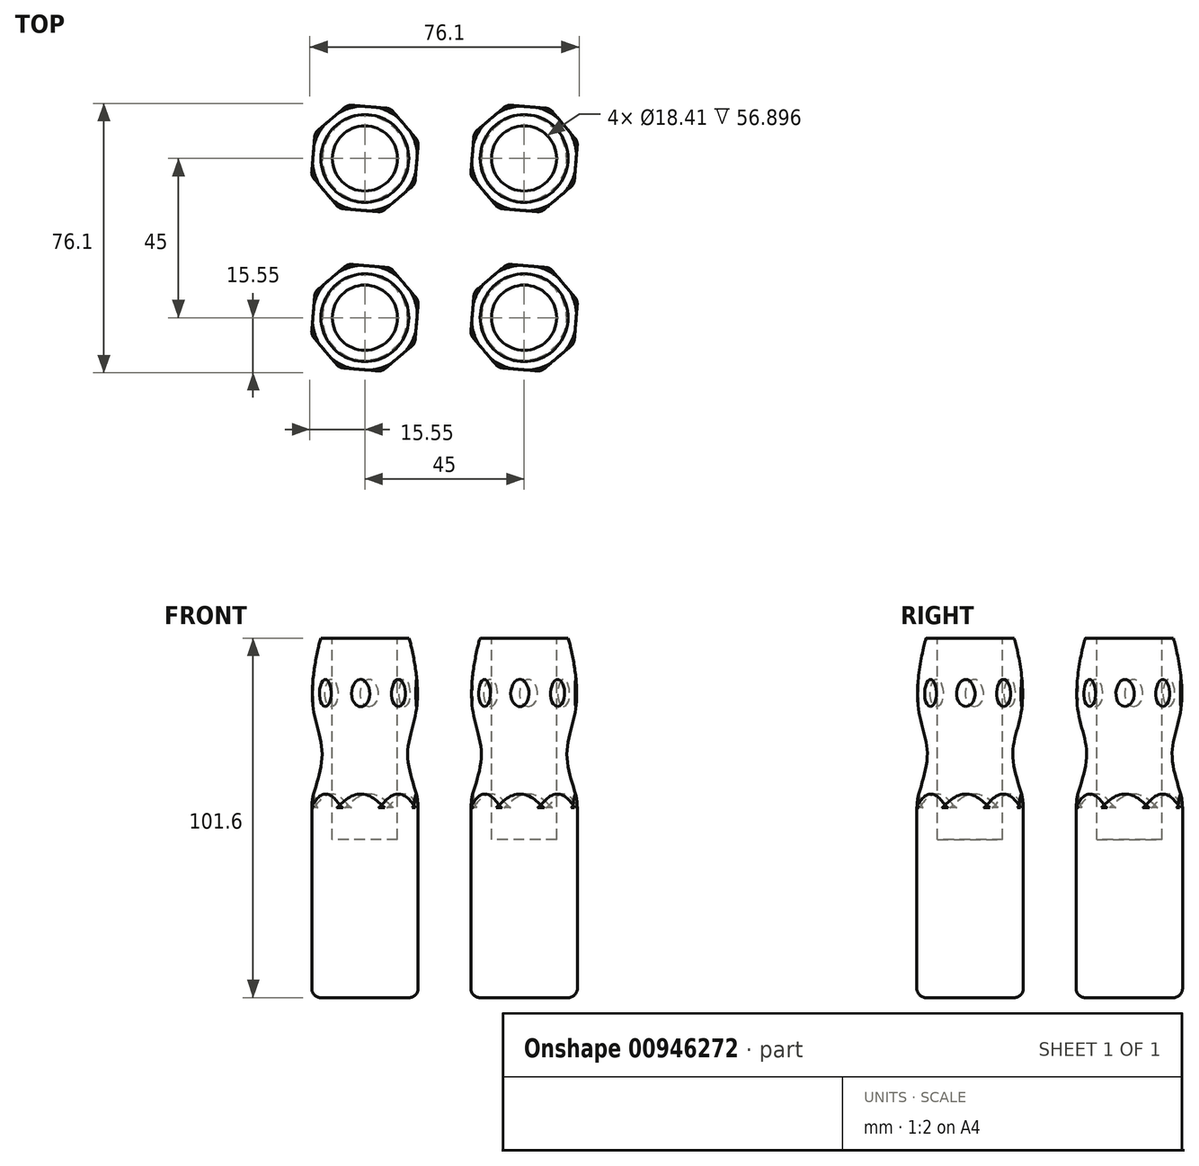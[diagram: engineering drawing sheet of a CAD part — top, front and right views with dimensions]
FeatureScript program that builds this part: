
annotation { "Feature Type Name" : "Feature", "Feature Type Description" : "" }
export const myFeature = defineFeature(function(context is Context, id is Id, definition is map)
    precondition{}
    {
        {
            var Q0;
            Q0=qCreatedBy(makeId("Top.planeOp"),FACE);
            var sketch = newSketch(context, id + "F0", { "sketchPlane" : qUnion([Q0])});
            skLineSegment(sketch, "E0.0", {"start": v(-4.85, 15.12) * mm, "end": v(7.26, 14.12) * mm});
            skLineSegment(sketch, "E0.1", {"start": v(7.26, 14.12) * mm, "end": v(15.12, 4.85) * mm});
            skLineSegment(sketch, "E0.2", {"start": v(15.12, 4.85) * mm, "end": v(14.12, -7.26) * mm});
            skLineSegment(sketch, "E0.3", {"start": v(14.12, -7.26) * mm, "end": v(4.85, -15.12) * mm});
            skLineSegment(sketch, "E0.4", {"start": v(4.85, -15.12) * mm, "end": v(-7.26, -14.12) * mm});
            skLineSegment(sketch, "E0.5", {"start": v(-7.26, -14.12) * mm, "end": v(-15.12, -4.85) * mm});
            skLineSegment(sketch, "E0.6", {"start": v(-15.12, -4.85) * mm, "end": v(-14.12, 7.26) * mm});
            skLineSegment(sketch, "E0.7", {"start": v(-14.12, 7.26) * mm, "end": v(-4.85, 15.12) * mm});
            skSolve(sketch);
        }
        {
            var Q0;
            Q0=makeQuery(id+"F0.imprint","IMPRINT",FACE,{"disambiguationData":[TD([[makeQuery(id+"F0.imprint","IMPRINT",EDGE,{"derivedFrom":sQuery(id+"F0.wireOp",EDGE,"e4fd1291-5814-49df-8d21-47046975691b.0")}),-1.0]])]});
            var Q1;
            Q1=makeQuery(id+"F0.imprint","IMPRINT",FACE,{"disambiguationData":[TD([[makeQuery(id+"F0.imprint","IMPRINT",EDGE,{"derivedFrom":sQuery(id+"F0.wireOp",EDGE,"E0.0")}),-1.0]])]});
            extrude(context, id + "F1", {"entities" : qUnion([Q0, Q1]), "depth" : 101.6 * mm, "offsetDistance" : 25.4 * mm});
        }
        {
            var Q0;
            Q0=qCreatedBy(makeId("Right.planeOp"),FACE);
            var sketch = newSketch(context, id + "F2", { "sketchPlane" : qUnion([Q0])});
            skLineSegment(sketch, "E1", {"start": v(0, 0) * mm, "end": v(-15.88, 0) * mm});
            skLineSegment(sketch, "E2", {"start": v(-15.88, 0) * mm, "end": v(-15.88, 53.34) * mm});
            skFitSpline(sketch, "E3", {"points": [v(-15.88, 53.34) * mm, v(-12.12, 69.77) * mm, v(-14.9, 85.44) * mm, v(-12.36, 101.7) * mm], "startDerivative": vector(18.24, 59.15) * mm, "endDerivative": vector(2.93, 2.79) * mm});
            skLineSegment(sketch, "E4", {"start": v(-12.36, 101.7) * mm, "end": v(-18.05, 101.7) * mm});
            skLineSegment(sketch, "E5", {"start": v(-18.05, 101.7) * mm, "end": v(-18.97, 0) * mm});
            skLineSegment(sketch, "E6", {"start": v(-18.97, 0) * mm, "end": v(-15.88, 0) * mm});
            skLineSegment(sketch, "E7", {"start": v(0, 0) * mm, "end": v(0, 84.28) * mm});
            skSolve(sketch);
        }
        {
            var Q0;
            Q0=makeQuery(id+"F2.imprint","IMPRINT",FACE,{"disambiguationData":[TD([[makeQuery(id+"F2.imprint","IMPRINT",EDGE,{"derivedFrom":sQuery(id+"F2.wireOp",EDGE,"E2")}),1.0]])]});
            var Q1;
            Q1=sQuery(id+"F2.wireOp",EDGE,"E7");
            revolve(context, id + "F3", {"operationType" : NewBodyOperationType.REMOVE, "surfaceOperationType" : NewSurfaceOperationType.NEW, "entities" : qUnion([Q0]), "axis" : qUnion([Q1]), "revolveType" : RevolveType.FULL, "oppositeDirection" : true});
        }
        {
            var Q0;
            Q0=makeQuery(id+"F1.opExtrude","CAP_FACE",FACE,{"disambiguationData":[OSD([sQuery(id+"F0.wireOp",EDGE,"E0.0"),sQuery(id+"F0.wireOp",EDGE,"E0.1"),sQuery(id+"F0.wireOp",EDGE,"E0.2"),sQuery(id+"F0.wireOp",EDGE,"E0.3"),sQuery(id+"F0.wireOp",EDGE,"E0.4"),sQuery(id+"F0.wireOp",EDGE,"E0.5"),sQuery(id+"F0.wireOp",EDGE,"E0.6"),sQuery(id+"F0.wireOp",EDGE,"E0.7")])],"isStart":false});
            var sketch = newSketch(context, id + "F4", { "sketchPlane" : qUnion([Q0])});
            skCircle(sketch, "E8.0.0", {"center": v(0, 0) * mm, "radius": 12.41 * mm});
            skCircle(sketch, "E9", {"center": v(0, 0) * mm, "radius": 9.2 * mm});
            skSolve(sketch);
        }
        {
            var Q0;
            Q0=makeQuery(id+"F4.imprint","IMPRINT",FACE,{"disambiguationData":[TD([[makeQuery(id+"F4.imprint","IMPRINT",EDGE,{"derivedFrom":sQuery(id+"F4.wireOp",EDGE,"E9")}),1.0]])]});
            extrude(context, id + "F5", {"entities" : qUnion([Q0]), "operationType" : NewBodyOperationType.REMOVE, "oppositeDirection" : true, "depth" : 56.9 * mm, "offsetDistance" : 25.4 * mm});
        }
        {
            var Q0;
            {var subQ0=sQuery(id+"F0.wireOp",EDGE,"E0.4");var subQ1=sQuery(id+"F0.wireOp",EDGE,"E0.3");var subQ2=sQuery(id+"F0.wireOp",EDGE,"E0.2");Q0=makeQuery(id+"F3.boolean.opBoolean","SPLIT",FACE,{"disambiguationData":[TD([makeQuery(id+"F1.opExtrude","CAP_FACE",FACE,{"disambiguationData":[OSD([sQuery(id+"F0.wireOp",EDGE,"E0.0"),sQuery(id+"F0.wireOp",EDGE,"E0.1"),subQ2,subQ1,subQ0,sQuery(id+"F0.wireOp",EDGE,"E0.5"),sQuery(id+"F0.wireOp",EDGE,"E0.6"),sQuery(id+"F0.wireOp",EDGE,"E0.7")])],"isStart":true}),makeQuery(id+"F1.opExtrude","SWEPT_FACE",FACE,{"disambiguationData":[OSD([subQ2])]}),makeQuery(id+"F1.opExtrude","SWEPT_FACE",FACE,{"disambiguationData":[OSD([subQ0])]}),makeQuery(id+"F3.opRevolve","SWEPT_FACE",FACE,{"disambiguationData":[OSD([sQuery(id+"F2.wireOp",EDGE,"E3")])]})])],"derivedFrom":makeQuery(id+"F1.opExtrude","SWEPT_FACE",FACE,{"disambiguationData":[OSD([subQ1])]})});}
            var Q1;
            {var subQ0=sQuery(id+"F0.wireOp",EDGE,"E0.5");var subQ1=sQuery(id+"F0.wireOp",EDGE,"E0.4");var subQ2=sQuery(id+"F0.wireOp",EDGE,"E0.3");Q1=makeQuery(id+"F3.boolean.opBoolean","SPLIT",FACE,{"disambiguationData":[TD([makeQuery(id+"F1.opExtrude","CAP_FACE",FACE,{"disambiguationData":[OSD([sQuery(id+"F0.wireOp",EDGE,"E0.0"),sQuery(id+"F0.wireOp",EDGE,"E0.1"),sQuery(id+"F0.wireOp",EDGE,"E0.2"),subQ2,subQ1,subQ0,sQuery(id+"F0.wireOp",EDGE,"E0.6"),sQuery(id+"F0.wireOp",EDGE,"E0.7")])],"isStart":true}),makeQuery(id+"F1.opExtrude","SWEPT_FACE",FACE,{"disambiguationData":[OSD([subQ2])]}),makeQuery(id+"F1.opExtrude","SWEPT_FACE",FACE,{"disambiguationData":[OSD([subQ0])]}),makeQuery(id+"F3.opRevolve","SWEPT_FACE",FACE,{"disambiguationData":[OSD([sQuery(id+"F2.wireOp",EDGE,"E3")])]})])],"derivedFrom":makeQuery(id+"F1.opExtrude","SWEPT_FACE",FACE,{"disambiguationData":[OSD([subQ1])]})});}
            var Q2;
            {var subQ0=sQuery(id+"F0.wireOp",EDGE,"E0.6");var subQ1=sQuery(id+"F0.wireOp",EDGE,"E0.5");var subQ2=sQuery(id+"F0.wireOp",EDGE,"E0.4");Q2=makeQuery(id+"F3.boolean.opBoolean","SPLIT",FACE,{"disambiguationData":[TD([makeQuery(id+"F1.opExtrude","CAP_FACE",FACE,{"disambiguationData":[OSD([sQuery(id+"F0.wireOp",EDGE,"E0.0"),sQuery(id+"F0.wireOp",EDGE,"E0.1"),sQuery(id+"F0.wireOp",EDGE,"E0.2"),sQuery(id+"F0.wireOp",EDGE,"E0.3"),subQ2,subQ1,subQ0,sQuery(id+"F0.wireOp",EDGE,"E0.7")])],"isStart":true}),makeQuery(id+"F1.opExtrude","SWEPT_FACE",FACE,{"disambiguationData":[OSD([subQ2])]}),makeQuery(id+"F1.opExtrude","SWEPT_FACE",FACE,{"disambiguationData":[OSD([subQ0])]}),makeQuery(id+"F3.opRevolve","SWEPT_FACE",FACE,{"disambiguationData":[OSD([sQuery(id+"F2.wireOp",EDGE,"E3")])]})])],"derivedFrom":makeQuery(id+"F1.opExtrude","SWEPT_FACE",FACE,{"disambiguationData":[OSD([subQ1])]})});}
            var Q3;
            {var subQ0=sQuery(id+"F0.wireOp",EDGE,"E0.7");var subQ1=sQuery(id+"F0.wireOp",EDGE,"E0.6");var subQ2=sQuery(id+"F0.wireOp",EDGE,"E0.5");Q3=makeQuery(id+"F3.boolean.opBoolean","SPLIT",FACE,{"disambiguationData":[TD([makeQuery(id+"F1.opExtrude","CAP_FACE",FACE,{"disambiguationData":[OSD([sQuery(id+"F0.wireOp",EDGE,"E0.0"),sQuery(id+"F0.wireOp",EDGE,"E0.1"),sQuery(id+"F0.wireOp",EDGE,"E0.2"),sQuery(id+"F0.wireOp",EDGE,"E0.3"),sQuery(id+"F0.wireOp",EDGE,"E0.4"),subQ2,subQ1,subQ0])],"isStart":true}),makeQuery(id+"F1.opExtrude","SWEPT_FACE",FACE,{"disambiguationData":[OSD([subQ2])]}),makeQuery(id+"F1.opExtrude","SWEPT_FACE",FACE,{"disambiguationData":[OSD([subQ0])]}),makeQuery(id+"F3.opRevolve","SWEPT_FACE",FACE,{"disambiguationData":[OSD([sQuery(id+"F2.wireOp",EDGE,"E3")])]})])],"derivedFrom":makeQuery(id+"F1.opExtrude","SWEPT_FACE",FACE,{"disambiguationData":[OSD([subQ1])]})});}
            var Q4;
            {var subQ0=sQuery(id+"F0.wireOp",EDGE,"E0.0");var subQ1=sQuery(id+"F0.wireOp",EDGE,"E0.7");var subQ2=sQuery(id+"F0.wireOp",EDGE,"E0.6");Q4=makeQuery(id+"F3.boolean.opBoolean","SPLIT",FACE,{"disambiguationData":[TD([makeQuery(id+"F1.opExtrude","SWEPT_FACE",FACE,{"disambiguationData":[OSD([subQ0])]}),makeQuery(id+"F1.opExtrude","CAP_FACE",FACE,{"disambiguationData":[OSD([subQ0,sQuery(id+"F0.wireOp",EDGE,"E0.1"),sQuery(id+"F0.wireOp",EDGE,"E0.2"),sQuery(id+"F0.wireOp",EDGE,"E0.3"),sQuery(id+"F0.wireOp",EDGE,"E0.4"),sQuery(id+"F0.wireOp",EDGE,"E0.5"),subQ2,subQ1])],"isStart":true}),makeQuery(id+"F1.opExtrude","SWEPT_FACE",FACE,{"disambiguationData":[OSD([subQ2])]}),makeQuery(id+"F3.opRevolve","SWEPT_FACE",FACE,{"disambiguationData":[OSD([sQuery(id+"F2.wireOp",EDGE,"E3")])]})])],"derivedFrom":makeQuery(id+"F1.opExtrude","SWEPT_FACE",FACE,{"disambiguationData":[OSD([subQ1])]})});}
            var Q5;
            {var subQ0=sQuery(id+"F0.wireOp",EDGE,"E0.7");var subQ1=sQuery(id+"F0.wireOp",EDGE,"E0.1");var subQ2=sQuery(id+"F0.wireOp",EDGE,"E0.0");Q5=makeQuery(id+"F3.boolean.opBoolean","SPLIT",FACE,{"disambiguationData":[TD([makeQuery(id+"F1.opExtrude","CAP_FACE",FACE,{"disambiguationData":[OSD([subQ2,subQ1,sQuery(id+"F0.wireOp",EDGE,"E0.2"),sQuery(id+"F0.wireOp",EDGE,"E0.3"),sQuery(id+"F0.wireOp",EDGE,"E0.4"),sQuery(id+"F0.wireOp",EDGE,"E0.5"),sQuery(id+"F0.wireOp",EDGE,"E0.6"),subQ0])],"isStart":true}),makeQuery(id+"F1.opExtrude","SWEPT_FACE",FACE,{"disambiguationData":[OSD([subQ1])]}),makeQuery(id+"F1.opExtrude","SWEPT_FACE",FACE,{"disambiguationData":[OSD([subQ0])]}),makeQuery(id+"F3.opRevolve","SWEPT_FACE",FACE,{"disambiguationData":[OSD([sQuery(id+"F2.wireOp",EDGE,"E3")])]})])],"derivedFrom":makeQuery(id+"F1.opExtrude","SWEPT_FACE",FACE,{"disambiguationData":[OSD([subQ2])]})});}
            var Q6;
            {var subQ0=sQuery(id+"F0.wireOp",EDGE,"E0.0");var subQ1=sQuery(id+"F0.wireOp",EDGE,"E0.2");var subQ2=sQuery(id+"F0.wireOp",EDGE,"E0.1");Q6=makeQuery(id+"F3.boolean.opBoolean","SPLIT",FACE,{"disambiguationData":[TD([makeQuery(id+"F1.opExtrude","SWEPT_FACE",FACE,{"disambiguationData":[OSD([subQ0])]}),makeQuery(id+"F1.opExtrude","CAP_FACE",FACE,{"disambiguationData":[OSD([subQ0,subQ2,subQ1,sQuery(id+"F0.wireOp",EDGE,"E0.3"),sQuery(id+"F0.wireOp",EDGE,"E0.4"),sQuery(id+"F0.wireOp",EDGE,"E0.5"),sQuery(id+"F0.wireOp",EDGE,"E0.6"),sQuery(id+"F0.wireOp",EDGE,"E0.7")])],"isStart":true}),makeQuery(id+"F1.opExtrude","SWEPT_FACE",FACE,{"disambiguationData":[OSD([subQ1])]}),makeQuery(id+"F3.opRevolve","SWEPT_FACE",FACE,{"disambiguationData":[OSD([sQuery(id+"F2.wireOp",EDGE,"E3")])]})])],"derivedFrom":makeQuery(id+"F1.opExtrude","SWEPT_FACE",FACE,{"disambiguationData":[OSD([subQ2])]})});}
            var Q7;
            {var subQ0=sQuery(id+"F0.wireOp",EDGE,"E0.3");var subQ1=sQuery(id+"F0.wireOp",EDGE,"E0.2");var subQ2=sQuery(id+"F0.wireOp",EDGE,"E0.1");Q7=makeQuery(id+"F3.boolean.opBoolean","SPLIT",FACE,{"disambiguationData":[TD([makeQuery(id+"F1.opExtrude","CAP_FACE",FACE,{"disambiguationData":[OSD([sQuery(id+"F0.wireOp",EDGE,"E0.0"),subQ2,subQ1,subQ0,sQuery(id+"F0.wireOp",EDGE,"E0.4"),sQuery(id+"F0.wireOp",EDGE,"E0.5"),sQuery(id+"F0.wireOp",EDGE,"E0.6"),sQuery(id+"F0.wireOp",EDGE,"E0.7")])],"isStart":true}),makeQuery(id+"F1.opExtrude","SWEPT_FACE",FACE,{"disambiguationData":[OSD([subQ2])]}),makeQuery(id+"F1.opExtrude","SWEPT_FACE",FACE,{"disambiguationData":[OSD([subQ0])]}),makeQuery(id+"F3.opRevolve","SWEPT_FACE",FACE,{"disambiguationData":[OSD([sQuery(id+"F2.wireOp",EDGE,"E3")])]})])],"derivedFrom":makeQuery(id+"F1.opExtrude","SWEPT_FACE",FACE,{"disambiguationData":[OSD([subQ1])]})});}
            fillet(context, id + "F6", {"entities" : qUnion([Q0, Q1, Q2, Q3, Q4, Q5, Q6, Q7]), "radius" : 2.54 * mm, "tangentPropagation" : true, "allowEdgeOverflow" : false});
        }
        {
            var Q0;
            Q0=makeQuery(id+"F1.opExtrude","SWEPT_BODY",BODY,{"disambiguationData":[OSD([sQuery(id+"F0.wireOp",EDGE,"E0.0"),sQuery(id+"F0.wireOp",EDGE,"E0.1"),sQuery(id+"F0.wireOp",EDGE,"E0.2"),sQuery(id+"F0.wireOp",EDGE,"E0.3"),sQuery(id+"F0.wireOp",EDGE,"E0.4"),sQuery(id+"F0.wireOp",EDGE,"E0.5"),sQuery(id+"F0.wireOp",EDGE,"E0.6"),sQuery(id+"F0.wireOp",EDGE,"E0.7")])]});
            transform(context, id + "F7", {"entities" : qUnion([Q0]), "transformType" : TransformType.TRANSLATION_3D, "dx" : 45 * mm, "dy" : 0 * mm, "dz" : 0 * mm, "makeCopy" : true});
        }
        {
            var Q0;
            Q0=makeQuery(id+"F1.opExtrude","SWEPT_BODY",BODY,{"disambiguationData":[OSD([sQuery(id+"F0.wireOp",EDGE,"E0.0"),sQuery(id+"F0.wireOp",EDGE,"E0.1"),sQuery(id+"F0.wireOp",EDGE,"E0.2"),sQuery(id+"F0.wireOp",EDGE,"E0.3"),sQuery(id+"F0.wireOp",EDGE,"E0.4"),sQuery(id+"F0.wireOp",EDGE,"E0.5"),sQuery(id+"F0.wireOp",EDGE,"E0.6"),sQuery(id+"F0.wireOp",EDGE,"E0.7")])]});
            var Q1;
            Q1=makeQuery(id+"F7.opPattern","COPY",BODY,{"derivedFrom":makeQuery(id+"F1.opExtrude","SWEPT_BODY",BODY,{"disambiguationData":[OSD([sQuery(id+"F0.wireOp",EDGE,"E0.0"),sQuery(id+"F0.wireOp",EDGE,"E0.1"),sQuery(id+"F0.wireOp",EDGE,"E0.2"),sQuery(id+"F0.wireOp",EDGE,"E0.3"),sQuery(id+"F0.wireOp",EDGE,"E0.4"),sQuery(id+"F0.wireOp",EDGE,"E0.5"),sQuery(id+"F0.wireOp",EDGE,"E0.6"),sQuery(id+"F0.wireOp",EDGE,"E0.7")])]}),"instanceName":"1"});
            transform(context, id + "F8", {"entities" : qUnion([Q0, Q1]), "transformType" : TransformType.TRANSLATION_3D, "dx" : 0 * mm, "dy" : 45 * mm, "dz" : 0 * mm, "makeCopy" : true});
        }
    });
